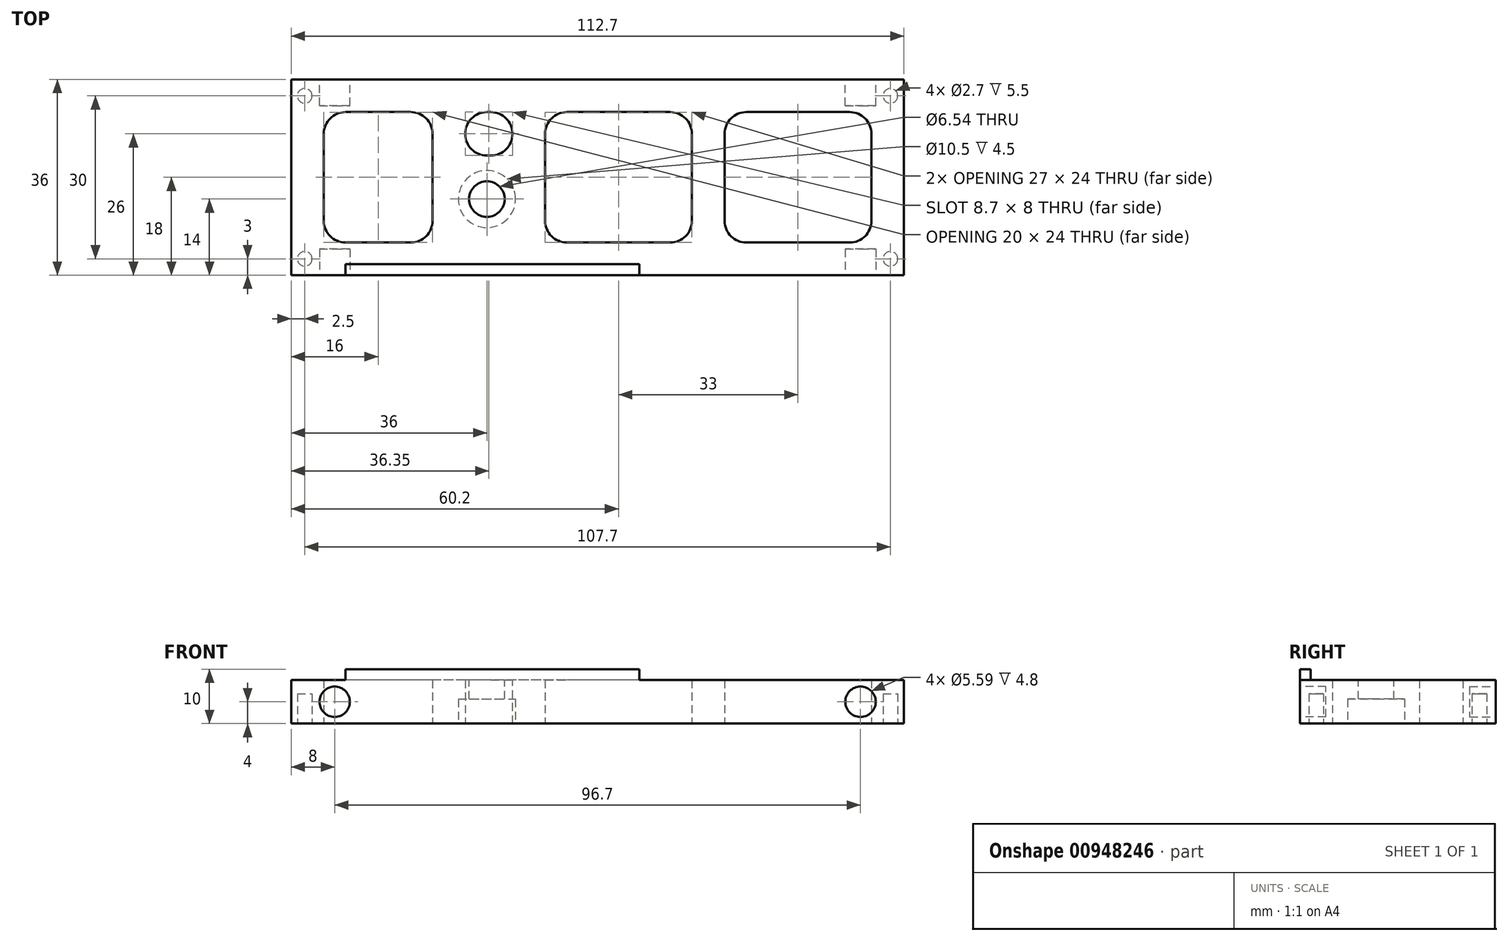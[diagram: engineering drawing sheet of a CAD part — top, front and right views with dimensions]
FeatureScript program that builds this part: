
annotation { "Feature Type Name" : "Feature", "Feature Type Description" : "" }
export const myFeature = defineFeature(function(context is Context, id is Id, definition is map)
    precondition{}
    {
        {
            var Q0;
            Q0=qCreatedBy(makeId("Top.planeOp"),FACE);
            var sketch = newSketch(context, id + "F0", { "sketchPlane" : qUnion([Q0])});
            skLineSegment(sketch, "E0.bottom", {"start": v(56.35, -18) * mm, "end": v(-56.35, -18) * mm});
            skLineSegment(sketch, "E0.top", {"start": v(56.35, 18) * mm, "end": v(-56.35, 18) * mm});
            skLineSegment(sketch, "E0.left", {"start": v(56.35, -18) * mm, "end": v(56.35, 18) * mm});
            skLineSegment(sketch, "E0.right", {"start": v(-56.35, -18) * mm, "end": v(-56.35, 18) * mm});
            skPoint(sketch, "E0.middle", {"position": v(0, 0) * mm});
            skSolve(sketch);
        }
        {
            var Q0;
            Q0=makeQuery(id+"F0.imprint","IMPRINT",FACE,{"disambiguationData":[TD([[makeQuery(id+"F0.imprint","IMPRINT",EDGE,{"derivedFrom":sQuery(id+"F0.wireOp",EDGE,"E0.bottom")}),-1.0]])]});
            extrude(context, id + "F1", {"entities" : qUnion([Q0]), "depth" : 8 * mm, "offsetDistance" : 25 * mm});
        }
        {
            var Q0;
            Q0=makeQuery(id+"F1.opExtrude","CAP_FACE",FACE,{"disambiguationData":[OSD([sQuery(id+"F0.wireOp",EDGE,"E0.bottom"),sQuery(id+"F0.wireOp",EDGE,"E0.top"),sQuery(id+"F0.wireOp",EDGE,"E0.left"),sQuery(id+"F0.wireOp",EDGE,"E0.right")])],"isStart":false});
            var sketch = newSketch(context, id + "F2", { "sketchPlane" : qUnion([Q0])});
            skSolve(sketch);
        }
        {
            var Q0;
            Q0=makeQuery(id+"F1.opExtrude","CAP_FACE",FACE,{"disambiguationData":[OSD([sQuery(id+"F0.wireOp",EDGE,"E0.bottom"),sQuery(id+"F0.wireOp",EDGE,"E0.top"),sQuery(id+"F0.wireOp",EDGE,"E0.left"),sQuery(id+"F0.wireOp",EDGE,"E0.right")])],"isStart":false});
            var sketch = newSketch(context, id + "F3", { "sketchPlane" : qUnion([Q0])});
            skLineSegment(sketch, "E1.bottom", {"start": v(7.65, -18) * mm, "end": v(-46.35, -18) * mm});
            skLineSegment(sketch, "E1.top", {"start": v(7.65, -16) * mm, "end": v(-46.35, -16) * mm});
            skLineSegment(sketch, "E1.left", {"start": v(7.65, -18) * mm, "end": v(7.65, -16) * mm});
            skLineSegment(sketch, "E1.right", {"start": v(-46.35, -18) * mm, "end": v(-46.35, -16) * mm});
            skSolve(sketch);
        }
        {
            var Q0;
            Q0 = qSketchRegion(id + "F3", true);
            extrude(context, id + "F4", {"entities" : qUnion([Q0]), "operationType" : NewBodyOperationType.ADD, "depth" : 2 * mm, "offsetDistance" : 25 * mm});
        }
        {
            var Q0;
            Q0=makeQuery(id+"F2.imprint","IMPRINT",FACE,{"disambiguationData":[TD([[makeQuery(id+"F2.imprint","IMPRINT",EDGE,{"derivedFrom":makeQuery(id+"F1.opExtrude","CAP_EDGE",EDGE,{"disambiguationData":[OSD([sQuery(id+"F0.wireOp",EDGE,"E0.bottom")])],"isStart":false})}),-1.0]])]});
            var sketch = newSketch(context, id + "F5", { "sketchPlane" : qUnion([Q0])});
            skCircle(sketch, "E2", {"center": v(-20.35, -4) * mm, "radius": 3.27 * mm});
            skLineSegment(sketch, "E3", {"start": v(-45.06, -4) * mm, "end": v(5.93, -4) * mm, "construction": true});
            skLineSegment(sketch, "E4", {"start": v(-20.35, -13.81) * mm, "end": v(-20.35, 11.8) * mm, "construction": true});
            skSolve(sketch);
        }
        {
            var Q0;
            Q0 = qSketchRegion(id + "F5", true);
            extrude(context, id + "F6", {"entities" : qUnion([Q0]), "operationType" : NewBodyOperationType.REMOVE, "endBound" : BoundingType.THROUGH_ALL, "oppositeDirection" : true, "depth" : 25 * mm, "offsetDistance" : 25 * mm});
        }
        {
            var Q0;
            Q0=makeQuery(id+"F1.opExtrude","CAP_FACE",FACE,{"disambiguationData":[OSD([sQuery(id+"F0.wireOp",EDGE,"E0.bottom"),sQuery(id+"F0.wireOp",EDGE,"E0.top"),sQuery(id+"F0.wireOp",EDGE,"E0.left"),sQuery(id+"F0.wireOp",EDGE,"E0.right")])],"isStart":true});
            var sketch = newSketch(context, id + "F7", { "sketchPlane" : qUnion([Q0])});
            skLineSegment(sketch, "E5", {"start": v(-65.19, 0) * mm, "end": v(58.26, 0) * mm, "construction": true});
            skLineSegment(sketch, "E6", {"start": v(0, 29.35) * mm, "end": v(0, -25.17) * mm, "construction": true});
            skPoint(sketch, "E6.endSnap0", {"position": v(0, -18) * mm});
            skCircle(sketch, "E7", {"center": v(-53.85, 15) * mm, "radius": 1.35 * mm});
            skCircle(sketch, "E8.0.1.0", {"center": v(-53.85, -15) * mm, "radius": 1.35 * mm});
            skCircle(sketch, "E8.1.0.0", {"center": v(53.85, 15) * mm, "radius": 1.35 * mm});
            skCircle(sketch, "E8.1.1.0", {"center": v(53.85, -15) * mm, "radius": 1.35 * mm});
            skLineSegment(sketch, "E8.direction1", {"start": v(-53.85, 15) * mm, "end": v(53.85, 15) * mm, "construction": true});
            skLineSegment(sketch, "E8.direction2", {"start": v(-53.85, 15) * mm, "end": v(-53.85, -15) * mm, "construction": true});
            skSolve(sketch);
        }
        {
            var Q0;
            Q0=makeQuery(id+"F7.imprint","IMPRINT",FACE,{"disambiguationData":[TD([[makeQuery(id+"F7.imprint","IMPRINT",EDGE,{"derivedFrom":sQuery(id+"F7.wireOp",EDGE,"E7")}),1.0]])]});
            var Q1;
            Q1=makeQuery(id+"F7.imprint","IMPRINT",FACE,{"disambiguationData":[TD([[makeQuery(id+"F7.imprint","IMPRINT",EDGE,{"derivedFrom":sQuery(id+"F7.wireOp",EDGE,"E8.0.1.0")}),1.0]])]});
            var Q2;
            Q2=makeQuery(id+"F7.imprint","IMPRINT",FACE,{"disambiguationData":[TD([[makeQuery(id+"F7.imprint","IMPRINT",EDGE,{"derivedFrom":sQuery(id+"F7.wireOp",EDGE,"E8.1.0.0")}),1.0]])]});
            var Q3;
            Q3=makeQuery(id+"F7.imprint","IMPRINT",FACE,{"disambiguationData":[TD([[makeQuery(id+"F7.imprint","IMPRINT",EDGE,{"derivedFrom":sQuery(id+"F7.wireOp",EDGE,"E8.1.1.0")}),1.0]])]});
            extrude(context, id + "F8", {"entities" : qUnion([Q0, Q1, Q2, Q3]), "operationType" : NewBodyOperationType.REMOVE, "oppositeDirection" : true, "depth" : 5.5 * mm, "offsetDistance" : 25 * mm});
        }
        {
            var Q0;
            Q0=makeQuery(id+"F1.opExtrude","CAP_FACE",FACE,{"disambiguationData":[OSD([sQuery(id+"F0.wireOp",EDGE,"E0.bottom"),sQuery(id+"F0.wireOp",EDGE,"E0.top"),sQuery(id+"F0.wireOp",EDGE,"E0.left"),sQuery(id+"F0.wireOp",EDGE,"E0.right")])],"isStart":true});
            var sketch = newSketch(context, id + "F9", { "sketchPlane" : qUnion([Q0])});
            skLineSegment(sketch, "E9.bottom", {"start": v(-50.35, 12) * mm, "end": v(-30.35, 12) * mm});
            skLineSegment(sketch, "E9.top", {"start": v(-50.35, -12) * mm, "end": v(-30.35, -12) * mm});
            skLineSegment(sketch, "E9.left", {"start": v(-50.35, 12) * mm, "end": v(-50.35, -12) * mm});
            skLineSegment(sketch, "E9.right", {"start": v(-30.35, 12) * mm, "end": v(-30.35, -12) * mm});
            skLineSegment(sketch, "E10.bottom", {"start": v(-9.65, 12) * mm, "end": v(17.35, 12) * mm});
            skLineSegment(sketch, "E10.top", {"start": v(-9.65, -12) * mm, "end": v(17.35, -12) * mm});
            skLineSegment(sketch, "E10.left", {"start": v(-9.65, 12) * mm, "end": v(-9.65, -12) * mm});
            skLineSegment(sketch, "E10.right", {"start": v(17.35, 12) * mm, "end": v(17.35, -12) * mm});
            skLineSegment(sketch, "E11.bottom", {"start": v(23.35, 12) * mm, "end": v(50.35, 12) * mm});
            skLineSegment(sketch, "E11.top", {"start": v(23.35, -12) * mm, "end": v(50.35, -12) * mm});
            skLineSegment(sketch, "E11.left", {"start": v(23.35, 12) * mm, "end": v(23.35, -12) * mm});
            skLineSegment(sketch, "E11.right", {"start": v(50.35, 12) * mm, "end": v(50.35, -12) * mm});
            skLineSegment(sketch, "E12.bottom", {"start": v(-24.35, -4) * mm, "end": v(-15.65, -4) * mm});
            skLineSegment(sketch, "E12.top", {"start": v(-24.35, -12) * mm, "end": v(-15.65, -12) * mm});
            skLineSegment(sketch, "E12.left", {"start": v(-24.35, -4) * mm, "end": v(-24.35, -12) * mm});
            skLineSegment(sketch, "E12.right", {"start": v(-15.65, -4) * mm, "end": v(-15.65, -12) * mm});
            skSolve(sketch);
        }
        {
            var Q0;
            Q0=makeQuery(id+"F9.imprint","IMPRINT",FACE,{"disambiguationData":[TD([[makeQuery(id+"F9.imprint","IMPRINT",EDGE,{"derivedFrom":sQuery(id+"F9.wireOp",EDGE,"E9.bottom")}),1.0]])]});
            var sketch = newSketch(context, id + "F10", { "sketchPlane" : qUnion([Q0])});
            skCircle(sketch, "E13", {"center": v(-20.35, 4) * mm, "radius": 5.25 * mm});
            skSolve(sketch);
        }
        {
            var Q0;
            Q0 = qSketchRegion(id + "F10", true);
            extrude(context, id + "F11", {"entities" : qUnion([Q0]), "operationType" : NewBodyOperationType.REMOVE, "oppositeDirection" : true, "depth" : 4.5 * mm, "offsetDistance" : 25 * mm});
        }
        {
            var Q0;
            Q0 = qSketchRegion(id + "F9", true);
            extrude(context, id + "F12", {"entities" : qUnion([Q0]), "operationType" : NewBodyOperationType.REMOVE, "endBound" : BoundingType.THROUGH_ALL, "oppositeDirection" : true, "depth" : 25 * mm, "offsetDistance" : 25 * mm});
        }
        {
            var Q0;
            Q0=makeQuery(id+"F12.boolean.opBoolean","COPY",EDGE,{"derivedFrom":makeQuery(id+"F12.opExtrude","SWEPT_EDGE",EDGE,{"disambiguationData":[OSD([sQuery(id+"F9.wireOp",EDGE,"E9.bottom"),sQuery(id+"F9.wireOp",EDGE,"E9.right")])]})});
            var Q1;
            Q1=makeQuery(id+"F12.boolean.opBoolean","COPY",EDGE,{"derivedFrom":makeQuery(id+"F12.opExtrude","SWEPT_EDGE",EDGE,{"disambiguationData":[OSD([sQuery(id+"F9.wireOp",EDGE,"E9.bottom"),sQuery(id+"F9.wireOp",EDGE,"E9.left")])]})});
            var Q2;
            Q2=makeQuery(id+"F12.boolean.opBoolean","COPY",EDGE,{"derivedFrom":makeQuery(id+"F12.opExtrude","SWEPT_EDGE",EDGE,{"disambiguationData":[OSD([sQuery(id+"F9.wireOp",EDGE,"E9.top"),sQuery(id+"F9.wireOp",EDGE,"E9.left")])]})});
            var Q3;
            Q3=makeQuery(id+"F12.boolean.opBoolean","COPY",EDGE,{"derivedFrom":makeQuery(id+"F12.opExtrude","SWEPT_EDGE",EDGE,{"disambiguationData":[OSD([sQuery(id+"F9.wireOp",EDGE,"E9.top"),sQuery(id+"F9.wireOp",EDGE,"E9.right")])]})});
            var Q4;
            Q4=makeQuery(id+"F12.boolean.opBoolean","COPY",EDGE,{"derivedFrom":makeQuery(id+"F12.opExtrude","SWEPT_EDGE",EDGE,{"disambiguationData":[OSD([sQuery(id+"F9.wireOp",EDGE,"E12.bottom"),sQuery(id+"F9.wireOp",EDGE,"E12.left")])]})});
            var Q5;
            Q5=makeQuery(id+"F12.boolean.opBoolean","COPY",EDGE,{"derivedFrom":makeQuery(id+"F12.opExtrude","SWEPT_EDGE",EDGE,{"disambiguationData":[OSD([sQuery(id+"F9.wireOp",EDGE,"E10.bottom"),sQuery(id+"F9.wireOp",EDGE,"E10.left")])]})});
            var Q6;
            Q6=makeQuery(id+"F12.boolean.opBoolean","COPY",EDGE,{"derivedFrom":makeQuery(id+"F12.opExtrude","SWEPT_EDGE",EDGE,{"disambiguationData":[OSD([sQuery(id+"F9.wireOp",EDGE,"E11.bottom"),sQuery(id+"F9.wireOp",EDGE,"E11.left")])]})});
            var Q7;
            Q7=makeQuery(id+"F12.boolean.opBoolean","COPY",EDGE,{"derivedFrom":makeQuery(id+"F12.opExtrude","SWEPT_EDGE",EDGE,{"disambiguationData":[OSD([sQuery(id+"F9.wireOp",EDGE,"E10.top"),sQuery(id+"F9.wireOp",EDGE,"E10.left")])]})});
            var Q8;
            Q8=makeQuery(id+"F12.boolean.opBoolean","COPY",EDGE,{"derivedFrom":makeQuery(id+"F12.opExtrude","SWEPT_EDGE",EDGE,{"disambiguationData":[OSD([sQuery(id+"F9.wireOp",EDGE,"E12.top"),sQuery(id+"F9.wireOp",EDGE,"E12.left")])]})});
            var Q9;
            Q9=makeQuery(id+"F12.boolean.opBoolean","COPY",EDGE,{"derivedFrom":makeQuery(id+"F12.opExtrude","SWEPT_EDGE",EDGE,{"disambiguationData":[OSD([sQuery(id+"F9.wireOp",EDGE,"E10.bottom"),sQuery(id+"F9.wireOp",EDGE,"E10.right")])]})});
            var Q10;
            Q10=makeQuery(id+"F12.boolean.opBoolean","COPY",EDGE,{"derivedFrom":makeQuery(id+"F12.opExtrude","SWEPT_EDGE",EDGE,{"disambiguationData":[OSD([sQuery(id+"F9.wireOp",EDGE,"E11.bottom"),sQuery(id+"F9.wireOp",EDGE,"E11.right")])]})});
            var Q11;
            Q11=makeQuery(id+"F12.boolean.opBoolean","COPY",EDGE,{"derivedFrom":makeQuery(id+"F12.opExtrude","SWEPT_EDGE",EDGE,{"disambiguationData":[OSD([sQuery(id+"F9.wireOp",EDGE,"E11.top"),sQuery(id+"F9.wireOp",EDGE,"E11.right")])]})});
            var Q12;
            Q12=makeQuery(id+"F12.boolean.opBoolean","COPY",EDGE,{"derivedFrom":makeQuery(id+"F12.opExtrude","SWEPT_EDGE",EDGE,{"disambiguationData":[OSD([sQuery(id+"F9.wireOp",EDGE,"E11.top"),sQuery(id+"F9.wireOp",EDGE,"E11.left")])]})});
            var Q13;
            Q13=makeQuery(id+"F12.boolean.opBoolean","COPY",EDGE,{"derivedFrom":makeQuery(id+"F12.opExtrude","SWEPT_EDGE",EDGE,{"disambiguationData":[OSD([sQuery(id+"F9.wireOp",EDGE,"E12.bottom"),sQuery(id+"F9.wireOp",EDGE,"E12.right")])]})});
            var Q14;
            Q14=makeQuery(id+"F12.boolean.opBoolean","COPY",EDGE,{"derivedFrom":makeQuery(id+"F12.opExtrude","SWEPT_EDGE",EDGE,{"disambiguationData":[OSD([sQuery(id+"F9.wireOp",EDGE,"E12.top"),sQuery(id+"F9.wireOp",EDGE,"E12.right")])]})});
            var Q15;
            Q15=makeQuery(id+"F12.boolean.opBoolean","COPY",EDGE,{"derivedFrom":makeQuery(id+"F12.opExtrude","SWEPT_EDGE",EDGE,{"disambiguationData":[OSD([sQuery(id+"F9.wireOp",EDGE,"E10.top"),sQuery(id+"F9.wireOp",EDGE,"E10.right")])]})});
            fillet(context, id + "F13", {"entities" : qUnion([Q0, Q1, Q2, Q3, Q4, Q5, Q6, Q7, Q8, Q9, Q10, Q11, Q12, Q13, Q14, Q15]), "radius" : 4 * mm, "tangentPropagation" : true, "allowEdgeOverflow" : false});
        }
        {
            var Q0;
            Q0=makeQuery(id+"F4.boolean.opBoolean","MERGE",FACE,{"derivedFrom":[makeQuery(id+"F1.opExtrude","SWEPT_FACE",FACE,{"disambiguationData":[OSD([sQuery(id+"F0.wireOp",EDGE,"E0.bottom")])]}),makeQuery(id+"F4.opExtrude","SWEPT_FACE",FACE,{"disambiguationData":[OSD([sQuery(id+"F3.wireOp",EDGE,"E1.bottom")])]})]});
            var sketch = newSketch(context, id + "F14", { "sketchPlane" : qUnion([Q0])});
            skCircle(sketch, "E14", {"center": v(-48.35, 4) * mm, "radius": 2.8 * mm});
            skPoint(sketch, "E14.centerSnap0", {"position": v(-56.35, 4) * mm});
            skCircle(sketch, "E15", {"center": v(48.35, 4) * mm, "radius": 2.8 * mm});
            skSolve(sketch);
        }
        {
            var Q0;
            Q0=makeQuery(id+"F14.imprint","IMPRINT",FACE,{"disambiguationData":[TD([[makeQuery(id+"F14.imprint","IMPRINT",EDGE,{"derivedFrom":sQuery(id+"F14.wireOp",EDGE,"E15")}),1.0]])]});
            var Q1;
            Q1=makeQuery(id+"F14.imprint","IMPRINT",FACE,{"disambiguationData":[TD([[makeQuery(id+"F14.imprint","IMPRINT",EDGE,{"derivedFrom":sQuery(id+"F14.wireOp",EDGE,"E14")}),1.0]])]});
            extrude(context, id + "F15", {"entities" : qUnion([Q0, Q1]), "operationType" : NewBodyOperationType.REMOVE, "oppositeDirection" : true, "depth" : 4.8 * mm, "offsetDistance" : 25 * mm});
        }
        {
            var Q0;
            Q0=makeQuery(id+"F1.opExtrude","SWEPT_FACE",FACE,{"disambiguationData":[OSD([sQuery(id+"F0.wireOp",EDGE,"E0.top")])]});
            var sketch = newSketch(context, id + "F16", { "sketchPlane" : qUnion([Q0])});
            skCircle(sketch, "E16", {"center": v(-48.35, 4) * mm, "radius": 2.8 * mm});
            skPoint(sketch, "E16.centerSnap0", {"position": v(-56.35, 4) * mm});
            skCircle(sketch, "E17", {"center": v(48.35, 4) * mm, "radius": 2.8 * mm});
            skPoint(sketch, "E17.centerSnap0", {"position": v(56.35, 4) * mm});
            skSolve(sketch);
        }
        {
            var Q0;
            Q0=makeQuery(id+"F16.imprint","IMPRINT",FACE,{"disambiguationData":[TD([[makeQuery(id+"F16.imprint","IMPRINT",EDGE,{"derivedFrom":sQuery(id+"F16.wireOp",EDGE,"E17")}),1.0]])]});
            var Q1;
            Q1=makeQuery(id+"F16.imprint","IMPRINT",FACE,{"disambiguationData":[TD([[makeQuery(id+"F16.imprint","IMPRINT",EDGE,{"derivedFrom":sQuery(id+"F16.wireOp",EDGE,"E16")}),1.0]])]});
            extrude(context, id + "F17", {"entities" : qUnion([Q0, Q1]), "operationType" : NewBodyOperationType.REMOVE, "oppositeDirection" : true, "depth" : 4.8 * mm, "offsetDistance" : 25 * mm});
        }
    });
